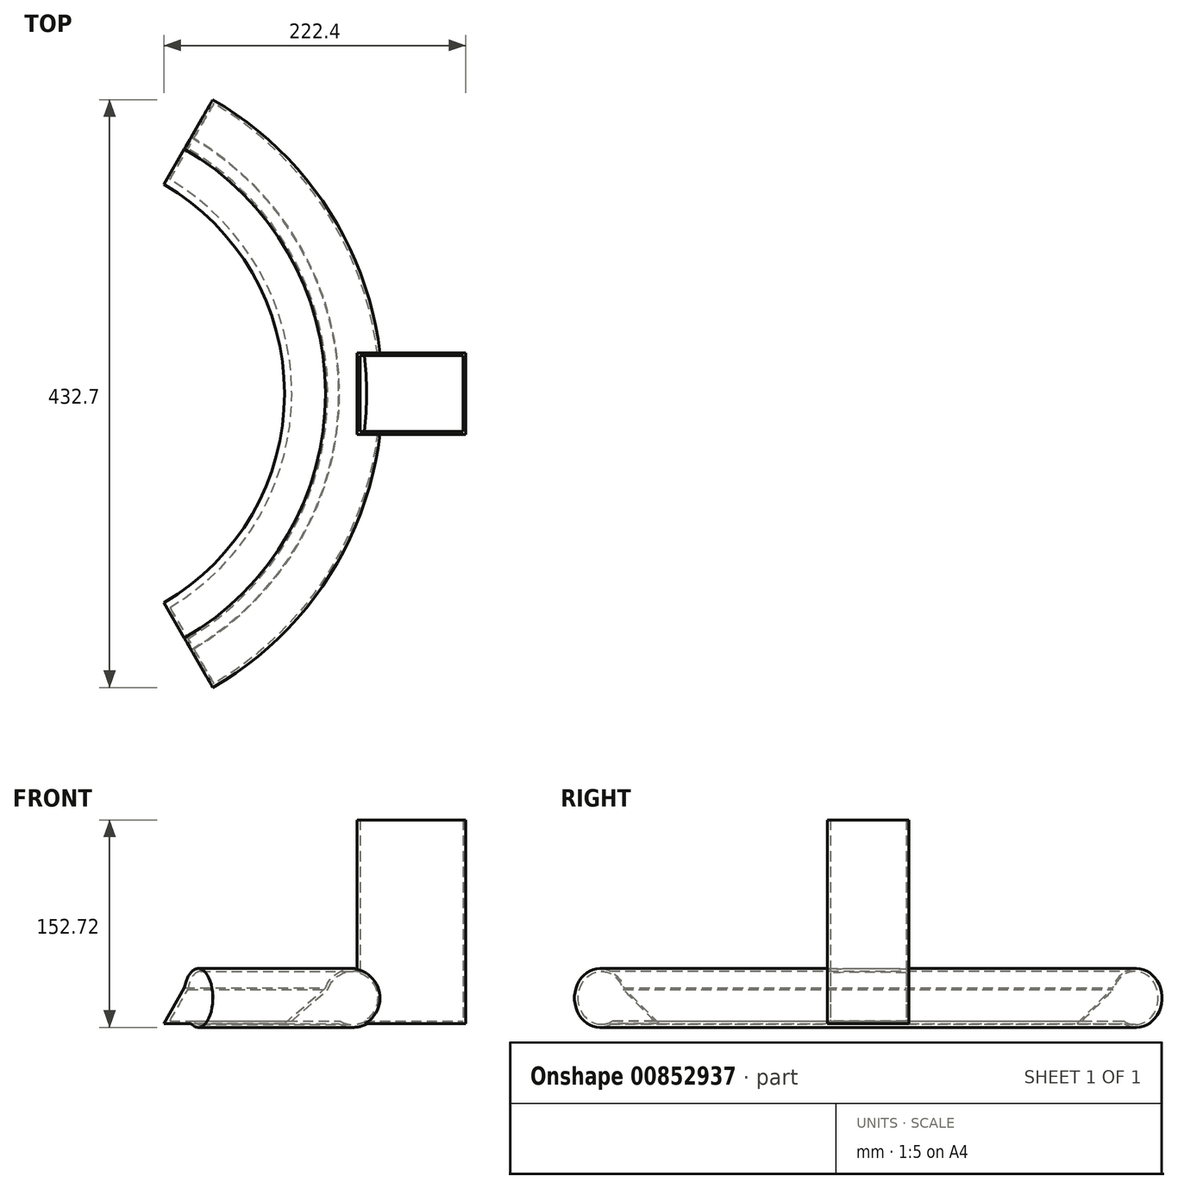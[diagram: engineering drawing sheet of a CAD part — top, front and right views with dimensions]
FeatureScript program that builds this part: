
annotation { "Feature Type Name" : "Feature", "Feature Type Description" : "" }
export const myFeature = defineFeature(function(context is Context, id is Id, definition is map)
    precondition{}
    {
        {
            var Q0;
            Q0=qCreatedBy(makeId("Front.planeOp"),FACE);
            var sketch = newSketch(context, id + "F0", { "sketchPlane" : qUnion([Q0])});
            skLineSegment(sketch, "E0", {"start": v(0, 0) * mm, "end": v(40, 0) * mm});
            skLineSegment(sketch, "E1", {"start": v(0, 0) * mm, "end": v(30.17, 26.27) * mm});
            skArc(sketch, "E2", {"start": v(40, 0) * mm, "mid": v(70.76, 26.49) * mm, "end": v(30.17, 26.27) * mm});
            skPoint(sketch, "E2.third.point", {"position": v(40, 0) * mm});
            skLineSegment(sketch, "E3", {"start": v(-177.7, 53.32) * mm, "end": v(-177.7, -55.4) * mm});
            skSolve(sketch);
        }
        {
            var Q0;
            {var subQ1=sQuery(id+"F0.wireOp",EDGE,"E1");var subQ4=sQuery(id+"F0.wireOp",EDGE,"E0");var subQ5=makeQuery(id+"F0.imprint","INTERSECT",VERTEX,{"derivedFrom":[subQ4,subQ1]});Q0=makeQuery(id+"F0.imprint","IMPRINT",FACE,{"disambiguationData":[TD([[makeQuery(id+"F0.imprint","IMPRINT",EDGE,{"disambiguationData":[TD([[subQ5,-1.0]])],"derivedFrom":subQ4}),1.0]])]});}
            var Q1;
            Q1=sQuery(id+"F0.wireOp",EDGE,"E3");
            revolve(context, id + "F1", {"surfaceOperationType" : NewSurfaceOperationType.NEW, "entities" : qUnion([Q0]), "axis" : qUnion([Q1]), "revolveType" : RevolveType.SYMMETRIC, "angle" : 120 * degree});
        }
        {
            var Q0;
            Q0=qCreatedBy(makeId("Top.planeOp"),FACE);
            var sketch = newSketch(context, id + "F2", { "sketchPlane" : qUnion([Q0])});
            skLineSegment(sketch, "E4.bottom", {"start": v(53.55, 30) * mm, "end": v(133.55, 30) * mm});
            skLineSegment(sketch, "E4.top", {"start": v(53.55, -30) * mm, "end": v(133.55, -30) * mm});
            skLineSegment(sketch, "E4.left", {"start": v(53.55, 30) * mm, "end": v(53.55, -30) * mm});
            skLineSegment(sketch, "E4.right", {"start": v(133.55, 30) * mm, "end": v(133.55, -30) * mm});
            skSolve(sketch);
        }
        {
            var Q0;
            Q0=makeQuery(id+"F2.imprint","IMPRINT",FACE,{"disambiguationData":[TD([[makeQuery(id+"F2.imprint","IMPRINT",EDGE,{"derivedFrom":sQuery(id+"F2.wireOp",EDGE,"E4.bottom")}),-1.0]])]});
            extrude(context, id + "F3", {"entities" : qUnion([Q0]), "operationType" : NewBodyOperationType.ADD, "depth" : 150 * mm, "offsetDistance" : 25 * mm});
        }
        {
            var Q0;
            Q0=makeQuery(id+"F3.opExtrude","CAP_FACE",FACE,{"disambiguationData":[OSD([sQuery(id+"F2.wireOp",EDGE,"E4.bottom"),sQuery(id+"F2.wireOp",EDGE,"E4.top"),sQuery(id+"F2.wireOp",EDGE,"E4.left"),sQuery(id+"F2.wireOp",EDGE,"E4.right")])],"isStart":false});
            shell(context, id + "F4", {"entities" : qUnion([Q0]), "thickness" : 2 * mm});
        }
    });
